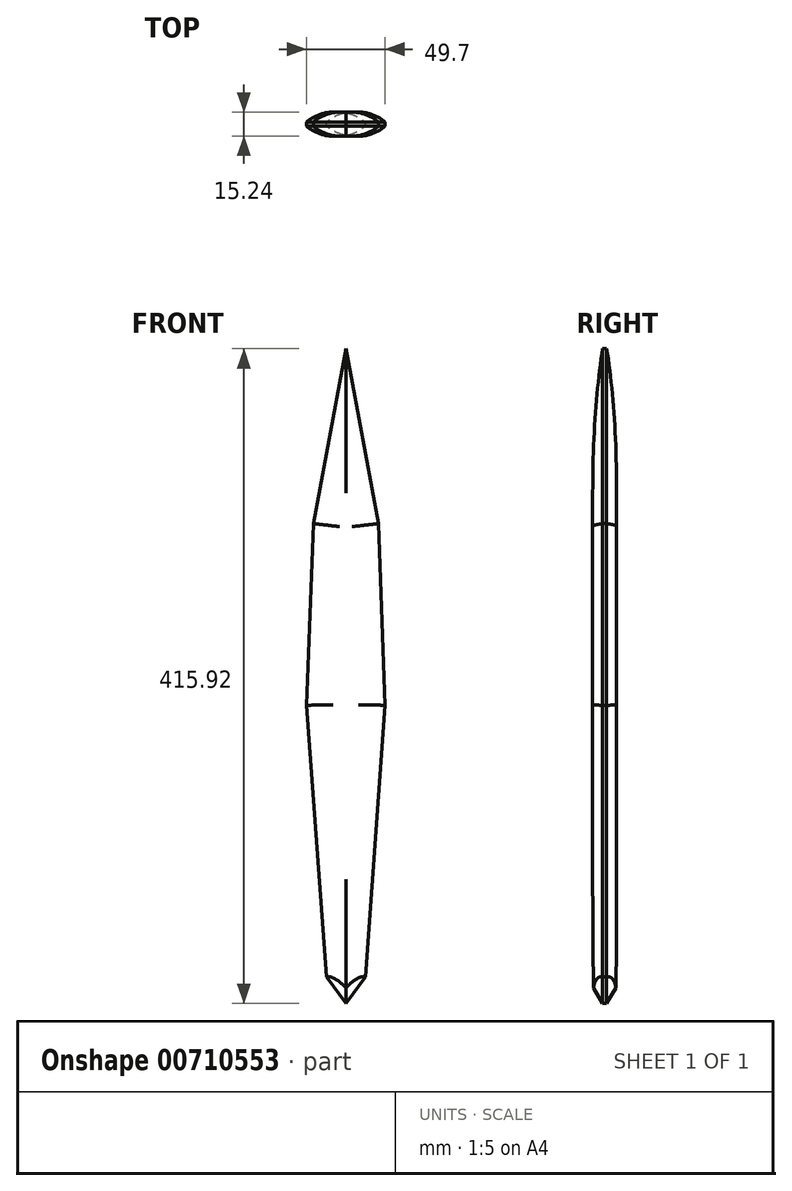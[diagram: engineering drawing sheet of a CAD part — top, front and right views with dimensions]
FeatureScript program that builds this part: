
annotation { "Feature Type Name" : "Feature", "Feature Type Description" : "" }
export const myFeature = defineFeature(function(context is Context, id is Id, definition is map)
    precondition{}
    {
        {
            var Q0;
            Q0=qCreatedBy(makeId("Front.planeOp"),FACE);
            var sketch = newSketch(context, id + "F0", { "sketchPlane" : qUnion([Q0])});
            skLineSegment(sketch, "E0", {"start": v(0, 404.37) * mm, "end": v(-20.72, 293.19) * mm});
            skLineSegment(sketch, "E1", {"start": v(-20.72, 293.19) * mm, "end": v(-24.85, 177.85) * mm});
            skLineSegment(sketch, "E2", {"start": v(-24.85, 177.85) * mm, "end": v(-17.57, 77.29) * mm});
            skLineSegment(sketch, "E3", {"start": v(-17.57, 77.29) * mm, "end": v(-12.37, 5.46) * mm});
            skLineSegment(sketch, "E4", {"start": v(-12.37, 5.46) * mm, "end": v(0, -11.55) * mm});
            skLineSegment(sketch, "E5", {"start": v(0, -11.55) * mm, "end": v(0, -7.73) * mm});
            skLineSegment(sketch, "E6.MirrorCS", {"start": v(12.37, 5.46) * mm, "end": v(0, -11.55) * mm});
            skLineSegment(sketch, "E7.MirrorCS", {"start": v(17.57, 77.29) * mm, "end": v(12.37, 5.46) * mm});
            skLineSegment(sketch, "E8.MirrorCS", {"start": v(24.85, 177.85) * mm, "end": v(17.57, 77.29) * mm});
            skLineSegment(sketch, "E9.MirrorCS", {"start": v(20.72, 293.19) * mm, "end": v(24.85, 177.85) * mm});
            skLineSegment(sketch, "E10.MirrorCS", {"start": v(0, 404.37) * mm, "end": v(20.72, 293.19) * mm});
            skSolve(sketch);
        }
        {
            var Q0;
            Q0=makeQuery(id+"F0.imprint","IMPRINT",FACE,{"disambiguationData":[TD([[makeQuery(id+"F0.imprint","IMPRINT",EDGE,{"derivedFrom":sQuery(id+"F0.wireOp",EDGE,"E0")}),1.0]])]});
            extrude(context, id + "F1", {"entities" : qUnion([Q0]), "depth" : 7.62 * mm, "offsetDistance" : 25.4 * mm});
        }
        {
            var Q0;
            Q0=makeQuery(id+"F1.opExtrude","CAP_FACE",FACE,{"disambiguationData":[OSD([sQuery(id+"F0.wireOp",EDGE,"E0"),sQuery(id+"F0.wireOp",EDGE,"E1"),sQuery(id+"F0.wireOp",EDGE,"E2"),sQuery(id+"F0.wireOp",EDGE,"E3"),sQuery(id+"F0.wireOp",EDGE,"E4"),sQuery(id+"F0.wireOp",EDGE,"E6.MirrorCS"),sQuery(id+"F0.wireOp",EDGE,"E7.MirrorCS"),sQuery(id+"F0.wireOp",EDGE,"E8.MirrorCS"),sQuery(id+"F0.wireOp",EDGE,"E9.MirrorCS"),sQuery(id+"F0.wireOp",EDGE,"E10.MirrorCS")])],"isStart":true});
            extrude(context, id + "F2", {"entities" : qUnion([Q0]), "operationType" : NewBodyOperationType.ADD, "depth" : 7.62 * mm, "offsetDistance" : 25.4 * mm});
        }
        {
            var Q0;
            Q0=makeQuery(id+"F1.opExtrude","CAP_FACE",FACE,{"disambiguationData":[OSD([sQuery(id+"F0.wireOp",EDGE,"E0"),sQuery(id+"F0.wireOp",EDGE,"E1"),sQuery(id+"F0.wireOp",EDGE,"E2"),sQuery(id+"F0.wireOp",EDGE,"E3"),sQuery(id+"F0.wireOp",EDGE,"E4"),sQuery(id+"F0.wireOp",EDGE,"E6.MirrorCS"),sQuery(id+"F0.wireOp",EDGE,"E7.MirrorCS"),sQuery(id+"F0.wireOp",EDGE,"E8.MirrorCS"),sQuery(id+"F0.wireOp",EDGE,"E9.MirrorCS"),sQuery(id+"F0.wireOp",EDGE,"E10.MirrorCS")])],"isStart":false});
            var Q1;
            Q1=makeQuery(id+"F2.opExtrude","CAP_FACE",FACE,{"disambiguationData":[OSD([sQuery(id+"F0.wireOp",EDGE,"E0"),sQuery(id+"F0.wireOp",EDGE,"E1"),sQuery(id+"F0.wireOp",EDGE,"E2"),sQuery(id+"F0.wireOp",EDGE,"E3"),sQuery(id+"F0.wireOp",EDGE,"E4"),sQuery(id+"F0.wireOp",EDGE,"E6.MirrorCS"),sQuery(id+"F0.wireOp",EDGE,"E7.MirrorCS"),sQuery(id+"F0.wireOp",EDGE,"E8.MirrorCS"),sQuery(id+"F0.wireOp",EDGE,"E9.MirrorCS"),sQuery(id+"F0.wireOp",EDGE,"E10.MirrorCS")])],"isStart":false});
            chamfer(context, id + "F3", {"entities" : qUnion([Q0, Q1]), "chamferType" : ChamferType.OFFSET_ANGLE, "width" : 6.35 * mm, "oppositeDirection" : false, "angle" : 45 * degree, "tangentPropagation" : true});
        }
        {
            var Q0;
            Q0=makeQuery(id+"F1.opExtrude","CAP_FACE",FACE,{"disambiguationData":[OSD([sQuery(id+"F0.wireOp",EDGE,"E0"),sQuery(id+"F0.wireOp",EDGE,"E1"),sQuery(id+"F0.wireOp",EDGE,"E2"),sQuery(id+"F0.wireOp",EDGE,"E3"),sQuery(id+"F0.wireOp",EDGE,"E4"),sQuery(id+"F0.wireOp",EDGE,"E6.MirrorCS"),sQuery(id+"F0.wireOp",EDGE,"E7.MirrorCS"),sQuery(id+"F0.wireOp",EDGE,"E8.MirrorCS"),sQuery(id+"F0.wireOp",EDGE,"E9.MirrorCS"),sQuery(id+"F0.wireOp",EDGE,"E10.MirrorCS")])],"isStart":false});
            var Q1;
            Q1=makeQuery(id+"F2.opExtrude","CAP_FACE",FACE,{"disambiguationData":[OSD([sQuery(id+"F0.wireOp",EDGE,"E0"),sQuery(id+"F0.wireOp",EDGE,"E1"),sQuery(id+"F0.wireOp",EDGE,"E2"),sQuery(id+"F0.wireOp",EDGE,"E3"),sQuery(id+"F0.wireOp",EDGE,"E4"),sQuery(id+"F0.wireOp",EDGE,"E6.MirrorCS"),sQuery(id+"F0.wireOp",EDGE,"E7.MirrorCS"),sQuery(id+"F0.wireOp",EDGE,"E8.MirrorCS"),sQuery(id+"F0.wireOp",EDGE,"E9.MirrorCS"),sQuery(id+"F0.wireOp",EDGE,"E10.MirrorCS")])],"isStart":false});
            fillet(context, id + "F4", {"entities" : qUnion([Q0, Q1]), "radius" : 25.4 * mm, "tangentPropagation" : true, "allowEdgeOverflow" : false});
        }
    });
